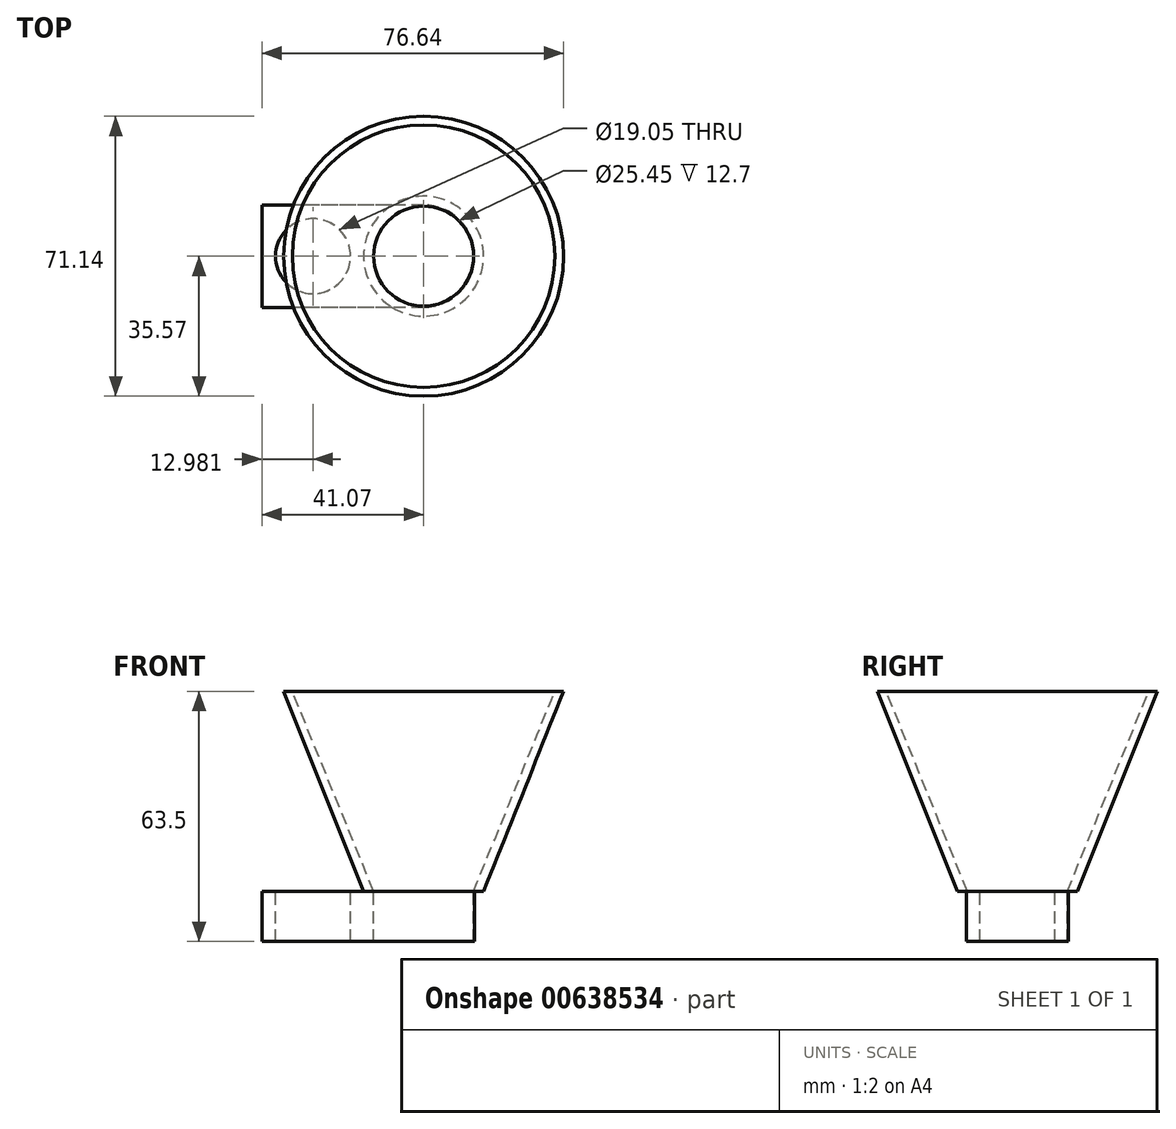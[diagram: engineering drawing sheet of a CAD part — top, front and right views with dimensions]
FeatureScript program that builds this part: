
annotation { "Feature Type Name" : "Feature", "Feature Type Description" : "" }
export const myFeature = defineFeature(function(context is Context, id is Id, definition is map)
    precondition{}
    {
        {
            var Q0;
            Q0=qCreatedBy(makeId("Top.planeOp"),FACE);
            var sketch = newSketch(context, id + "F0", { "sketchPlane" : qUnion([Q0])});
            skCircle(sketch, "E0", {"center": v(0, 0) * mm, "radius": 35.57 * mm});
            skSolve(sketch);
        }
        {
            var Q0;
            Q0=qCreatedBy(makeId("Top.planeOp"),FACE);
            cPlane(context, id + "F1", {"entities" : qUnion([Q0]), "cplaneType" : CPlaneType.OFFSET, "offset" : 50.8 * mm, "oppositeDirection" : true, "width" : 152.4 * mm, "height" : 152.4 * mm});
        }
        {
            var Q0;
            Q0=qCreatedBy(id+"F1.planeOp",FACE);
            var sketch = newSketch(context, id + "F2", { "sketchPlane" : qUnion([Q0])});
            skCircle(sketch, "E1", {"center": v(0, 0) * mm, "radius": 15.24 * mm});
            skSolve(sketch);
        }
        {
            var Q0;
            Q0=makeQuery(id+"F0.imprint","IMPRINT",FACE,{"disambiguationData":[TD([[makeQuery(id+"F0.imprint","IMPRINT",EDGE,{"derivedFrom":sQuery(id+"F0.wireOp",EDGE,"E0")}),1.0]])]});
            var Q1;
            Q1=makeQuery(id+"F2.imprint","IMPRINT",FACE,{"disambiguationData":[TD([[makeQuery(id+"F2.imprint","IMPRINT",EDGE,{"derivedFrom":sQuery(id+"F2.wireOp",EDGE,"E1")}),1.0]])]});
            loft(context, id + "F3", {"sheetProfilesArray" : [{ "sheetProfileEntities" : qUnion([Q0]) }, { "sheetProfileEntities" : qUnion([Q1]) }]});
        }
        {
            var Q0;
            Q0=qCreatedBy(makeId("Top.planeOp"),FACE);
            var sketch = newSketch(context, id + "F4", { "sketchPlane" : qUnion([Q0])});
            skCircle(sketch, "E2", {"center": v(0, 0) * mm, "radius": 33.35 * mm});
            skSolve(sketch);
        }
        {
            var Q0;
            Q0=qCreatedBy(id+"F1.planeOp",FACE);
            var sketch = newSketch(context, id + "F5", { "sketchPlane" : qUnion([Q0])});
            skCircle(sketch, "E3", {"center": v(0, 0) * mm, "radius": 12.7 * mm});
            skSolve(sketch);
        }
        {
            var Q1;
            Q1=makeQuery(id+"F4.imprint","IMPRINT",FACE,{"disambiguationData":[TD([[makeQuery(id+"F4.imprint","IMPRINT",EDGE,{"derivedFrom":sQuery(id+"F4.wireOp",EDGE,"E2")}),1.0]])]});
            var Q2;
            Q2=makeQuery(id+"F5.imprint","IMPRINT",FACE,{"disambiguationData":[TD([[makeQuery(id+"F5.imprint","IMPRINT",EDGE,{"derivedFrom":sQuery(id+"F5.wireOp",EDGE,"E3")}),1.0]])]});
            loft(context, id + "F6", {"operationType" : NewBodyOperationType.REMOVE, "sheetProfilesArray" : [{ "sheetProfileEntities" : qUnion([Q1]) }, { "sheetProfileEntities" : qUnion([Q2]) }]});
        }
        {
            var Q0;
            Q0=qCreatedBy(id+"F1.planeOp",FACE);
            var sketch = newSketch(context, id + "F7", { "sketchPlane" : qUnion([Q0])});
            skArc(sketch, "E4", {"start": v(0, -12.99) * mm, "mid": v(12.99, 0) * mm, "end": v(0, 12.99) * mm});
            skLineSegment(sketch, "E5", {"start": v(0, -12.99) * mm, "end": v(-41.07, -12.99) * mm});
            skLineSegment(sketch, "E6", {"start": v(0, 12.99) * mm, "end": v(-41.07, 12.99) * mm});
            skLineSegment(sketch, "E7", {"start": v(-41.07, -12.99) * mm, "end": v(-41.07, 12.99) * mm});
            skCircle(sketch, "E8", {"center": v(-28.09, 0) * mm, "radius": 9.53 * mm});
            skPoint(sketch, "E8.centerSnap0", {"position": v(-41.07, 0) * mm});
            skArc(sketch, "E9", {"start": v(-0.35, -12.99) * mm, "mid": v(13, 0) * mm, "end": v(-0.35, 12.99) * mm});
            skCircle(sketch, "E10", {"center": v(0, 0) * mm, "radius": 12.72 * mm});
            skSolve(sketch);
        }
        {
            var Q0;
            {var subQ1=sQuery(id+"F7.wireOp",EDGE,"E4");Q0=makeQuery(id+"F7.imprint","IMPRINT",FACE,{"disambiguationData":[TD([[makeQuery(id+"F7.imprint","IMPRINT",EDGE,{"derivedFrom":subQ1}),1.0]])]});}
            extrude(context, id + "F8", {"entities" : qUnion([Q0]), "operationType" : NewBodyOperationType.ADD, "oppositeDirection" : true, "depth" : 12.7 * mm, "offsetDistance" : 25.4 * mm});
        }
    });
